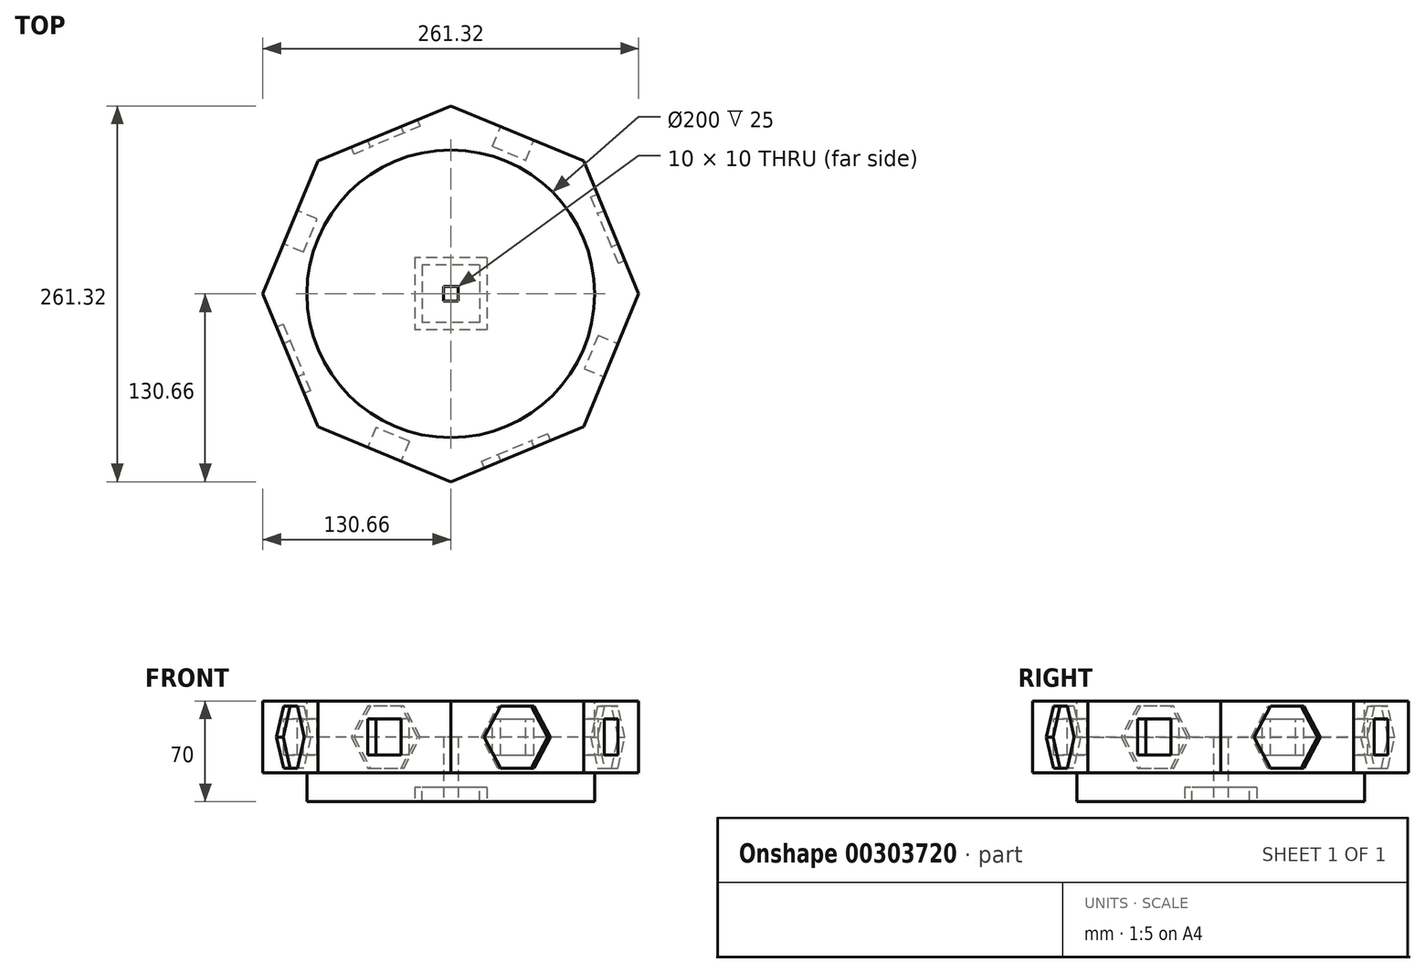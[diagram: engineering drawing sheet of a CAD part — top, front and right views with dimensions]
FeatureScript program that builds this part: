
annotation { "Feature Type Name" : "Feature", "Feature Type Description" : "" }
export const myFeature = defineFeature(function(context is Context, id is Id, definition is map)
    precondition{}
    {
        {
            var Q0;
            Q0=qCreatedBy(makeId("Top.planeOp"),FACE);
            var sketch = newSketch(context, id + "F0", { "sketchPlane" : qUnion([Q0])});
            skCircle(sketch, "E0.cCircle", {"center": v(0, 0) * mm, "radius": 130.66 * mm, "construction": true});
            skLineSegment(sketch, "E0.0", {"start": v(0, -130.66) * mm, "end": v(-92.39, -92.39) * mm});
            skLineSegment(sketch, "E0.1", {"start": v(-92.39, -92.39) * mm, "end": v(-130.66, 0) * mm});
            skLineSegment(sketch, "E0.2", {"start": v(-130.66, 0) * mm, "end": v(-92.39, 92.39) * mm});
            skLineSegment(sketch, "E0.3", {"start": v(-92.39, 92.39) * mm, "end": v(0, 130.66) * mm});
            skLineSegment(sketch, "E0.4", {"start": v(0, 130.66) * mm, "end": v(92.39, 92.39) * mm});
            skLineSegment(sketch, "E0.5", {"start": v(92.39, 92.39) * mm, "end": v(130.66, 0) * mm});
            skLineSegment(sketch, "E0.6", {"start": v(130.66, 0) * mm, "end": v(92.39, -92.39) * mm});
            skLineSegment(sketch, "E0.7", {"start": v(92.39, -92.39) * mm, "end": v(0, -130.66) * mm});
            skSolve(sketch);
        }
        {
            var Q0;
            Q0=makeQuery(id+"F0.imprint","IMPRINT",FACE,{"disambiguationData":[TD([[makeQuery(id+"F0.imprint","IMPRINT",EDGE,{"derivedFrom":sQuery(id+"F0.wireOp",EDGE,"E0.0")}),-1.0]])]});
            extrude(context, id + "F1", {"entities" : qUnion([Q0]), "depth" : 50 * mm});
        }
        {
            var Q0;
            Q0=makeQuery(id+"F1.opExtrude","SWEPT_FACE",FACE,{"disambiguationData":[OSD([sQuery(id+"F0.wireOp",EDGE,"E0.0")])]});
            var sketch = newSketch(context, id + "F2", { "sketchPlane" : qUnion([Q0])});
            skLineSegment(sketch, "E1.bottom", {"start": v(12.5, 12.5) * mm, "end": v(-12.5, 12.5) * mm});
            skLineSegment(sketch, "E1.top", {"start": v(12.5, 37.5) * mm, "end": v(-12.5, 37.5) * mm});
            skLineSegment(sketch, "E1.left", {"start": v(12.5, 12.5) * mm, "end": v(12.5, 37.5) * mm});
            skLineSegment(sketch, "E1.right", {"start": v(-12.5, 12.5) * mm, "end": v(-12.5, 37.5) * mm});
            skPoint(sketch, "E1.middle", {"position": v(0, 25) * mm});
            skPoint(sketch, "E1.middle.positionSnap0", {"position": v(-50, 25) * mm});
            skPoint(sketch, "E1.centerSnap0", {"position": v(-50, 25) * mm});
            skSolve(sketch);
        }
        {
            var Q0;
            Q0=makeQuery(id+"F2.imprint","IMPRINT",FACE,{"disambiguationData":[TD([[makeQuery(id+"F2.imprint","IMPRINT",EDGE,{"derivedFrom":sQuery(id+"F2.wireOp",EDGE,"E1.bottom")}),-1.0]])]});
            extrude(context, id + "F3", {"entities" : qUnion([Q0]), "operationType" : NewBodyOperationType.REMOVE, "oppositeDirection" : true, "depth" : 15 * mm});
        }
        {
            var Q0;
            Q0=makeQuery(id+"F1.opExtrude","SWEPT_FACE",FACE,{"disambiguationData":[OSD([sQuery(id+"F0.wireOp",EDGE,"E0.2")])]});
            var sketch = newSketch(context, id + "F4", { "sketchPlane" : qUnion([Q0])});
            skLineSegment(sketch, "E2.bottom", {"start": v(12.5, 12.5) * mm, "end": v(-12.5, 12.5) * mm});
            skLineSegment(sketch, "E2.top", {"start": v(12.5, 37.5) * mm, "end": v(-12.5, 37.5) * mm});
            skLineSegment(sketch, "E2.left", {"start": v(12.5, 12.5) * mm, "end": v(12.5, 37.5) * mm});
            skLineSegment(sketch, "E2.right", {"start": v(-12.5, 12.5) * mm, "end": v(-12.5, 37.5) * mm});
            skPoint(sketch, "E2.middle", {"position": v(0, 25) * mm});
            skPoint(sketch, "E2.middle.positionSnap0", {"position": v(-50, 25) * mm});
            skPoint(sketch, "E2.centerSnap0", {"position": v(-50, 25) * mm});
            skSolve(sketch);
        }
        {
            var Q0;
            Q0=makeQuery(id+"F4.imprint","IMPRINT",FACE,{"disambiguationData":[TD([[makeQuery(id+"F4.imprint","IMPRINT",EDGE,{"derivedFrom":sQuery(id+"F4.wireOp",EDGE,"E2.bottom")}),-1.0]])]});
            extrude(context, id + "F5", {"entities" : qUnion([Q0]), "operationType" : NewBodyOperationType.REMOVE, "oppositeDirection" : true, "depth" : 15 * mm});
        }
        {
            var Q0;
            Q0=makeQuery(id+"F1.opExtrude","SWEPT_FACE",FACE,{"disambiguationData":[OSD([sQuery(id+"F0.wireOp",EDGE,"E0.4")])]});
            var sketch = newSketch(context, id + "F6", { "sketchPlane" : qUnion([Q0])});
            skLineSegment(sketch, "E3.bottom", {"start": v(12.5, 12.5) * mm, "end": v(-12.5, 12.5) * mm});
            skLineSegment(sketch, "E3.top", {"start": v(12.5, 37.5) * mm, "end": v(-12.5, 37.5) * mm});
            skLineSegment(sketch, "E3.left", {"start": v(12.5, 12.5) * mm, "end": v(12.5, 37.5) * mm});
            skLineSegment(sketch, "E3.right", {"start": v(-12.5, 12.5) * mm, "end": v(-12.5, 37.5) * mm});
            skPoint(sketch, "E3.middle", {"position": v(0, 25) * mm});
            skPoint(sketch, "E3.middle.positionSnap0", {"position": v(-50, 25) * mm});
            skPoint(sketch, "E3.centerSnap0", {"position": v(-50, 25) * mm});
            skSolve(sketch);
        }
        {
            var Q0;
            Q0=makeQuery(id+"F6.imprint","IMPRINT",FACE,{"disambiguationData":[TD([[makeQuery(id+"F6.imprint","IMPRINT",EDGE,{"derivedFrom":sQuery(id+"F6.wireOp",EDGE,"E3.bottom")}),-1.0]])]});
            extrude(context, id + "F7", {"entities" : qUnion([Q0]), "operationType" : NewBodyOperationType.REMOVE, "oppositeDirection" : true, "depth" : 15 * mm});
        }
        {
            var Q0;
            Q0=makeQuery(id+"F1.opExtrude","SWEPT_FACE",FACE,{"disambiguationData":[OSD([sQuery(id+"F0.wireOp",EDGE,"E0.6")])]});
            var sketch = newSketch(context, id + "F8", { "sketchPlane" : qUnion([Q0])});
            skLineSegment(sketch, "E4.bottom", {"start": v(12.5, 12.5) * mm, "end": v(-12.5, 12.5) * mm});
            skLineSegment(sketch, "E4.top", {"start": v(12.5, 37.5) * mm, "end": v(-12.5, 37.5) * mm});
            skLineSegment(sketch, "E4.left", {"start": v(12.5, 12.5) * mm, "end": v(12.5, 37.5) * mm});
            skLineSegment(sketch, "E4.right", {"start": v(-12.5, 12.5) * mm, "end": v(-12.5, 37.5) * mm});
            skPoint(sketch, "E4.middle", {"position": v(0, 25) * mm});
            skPoint(sketch, "E4.middle.positionSnap0", {"position": v(-50, 25) * mm});
            skPoint(sketch, "E4.centerSnap0", {"position": v(-50, 25) * mm});
            skSolve(sketch);
        }
        {
            var Q0;
            Q0=makeQuery(id+"F8.imprint","IMPRINT",FACE,{"disambiguationData":[TD([[makeQuery(id+"F8.imprint","IMPRINT",EDGE,{"derivedFrom":sQuery(id+"F8.wireOp",EDGE,"E4.bottom")}),-1.0]])]});
            extrude(context, id + "F9", {"entities" : qUnion([Q0]), "operationType" : NewBodyOperationType.REMOVE, "oppositeDirection" : true, "depth" : 15 * mm});
        }
        {
            var Q0;
            Q0=makeQuery(id+"F1.opExtrude","SWEPT_FACE",FACE,{"disambiguationData":[OSD([sQuery(id+"F0.wireOp",EDGE,"E0.7")])]});
            var sketch = newSketch(context, id + "F10", { "sketchPlane" : qUnion([Q0])});
            skCircle(sketch, "E5.cCircle", {"center": v(0, 25) * mm, "radius": 21.65 * mm, "construction": true});
            skPoint(sketch, "E5.cCircle.centerSnap0", {"position": v(-50, 25) * mm});
            skLineSegment(sketch, "E5.0", {"start": v(25, 25) * mm, "end": v(12.5, 3.35) * mm});
            skLineSegment(sketch, "E5.1", {"start": v(12.5, 3.35) * mm, "end": v(-12.5, 3.35) * mm});
            skLineSegment(sketch, "E5.2", {"start": v(-12.5, 3.35) * mm, "end": v(-25, 25) * mm});
            skLineSegment(sketch, "E5.3", {"start": v(-25, 25) * mm, "end": v(-12.5, 46.65) * mm});
            skLineSegment(sketch, "E5.4", {"start": v(-12.5, 46.65) * mm, "end": v(12.5, 46.65) * mm});
            skLineSegment(sketch, "E5.5", {"start": v(12.5, 46.65) * mm, "end": v(25, 25) * mm});
            skPoint(sketch, "E5.0.midPoint", {"position": v(18.75, 14.17) * mm});
            skSolve(sketch);
        }
        {
            var Q0;
            Q0=makeQuery(id+"F10.imprint","IMPRINT",FACE,{"disambiguationData":[TD([[makeQuery(id+"F10.imprint","IMPRINT",EDGE,{"derivedFrom":sQuery(id+"F10.wireOp",EDGE,"E5.0")}),-1.0]])]});
            extrude(context, id + "F11", {"entities" : qUnion([Q0]), "operationType" : NewBodyOperationType.REMOVE, "oppositeDirection" : true, "depth" : 5 * mm});
        }
        {
            var Q0;
            Q0=makeQuery(id+"F1.opExtrude","SWEPT_FACE",FACE,{"disambiguationData":[OSD([sQuery(id+"F0.wireOp",EDGE,"E0.5")])]});
            var sketch = newSketch(context, id + "F12", { "sketchPlane" : qUnion([Q0])});
            skCircle(sketch, "E6.cCircle", {"center": v(0, 25) * mm, "radius": 21.65 * mm, "construction": true});
            skPoint(sketch, "E6.cCircle.centerSnap0", {"position": v(0, 50) * mm});
            skPoint(sketch, "E6.cCircle.centerSnap1", {"position": v(-50, 25) * mm});
            skLineSegment(sketch, "E6.0", {"start": v(25, 25) * mm, "end": v(12.5, 3.35) * mm});
            skLineSegment(sketch, "E6.1", {"start": v(12.5, 3.35) * mm, "end": v(-12.5, 3.35) * mm});
            skLineSegment(sketch, "E6.2", {"start": v(-12.5, 3.35) * mm, "end": v(-25, 25) * mm});
            skLineSegment(sketch, "E6.3", {"start": v(-25, 25) * mm, "end": v(-12.5, 46.65) * mm});
            skLineSegment(sketch, "E6.4", {"start": v(-12.5, 46.65) * mm, "end": v(12.5, 46.65) * mm});
            skLineSegment(sketch, "E6.5", {"start": v(12.5, 46.65) * mm, "end": v(25, 25) * mm});
            skPoint(sketch, "E6.0.midPoint", {"position": v(18.75, 14.17) * mm});
            skSolve(sketch);
        }
        {
            var Q0;
            Q0=makeQuery(id+"F12.imprint","IMPRINT",FACE,{"disambiguationData":[TD([[makeQuery(id+"F12.imprint","IMPRINT",EDGE,{"derivedFrom":sQuery(id+"F12.wireOp",EDGE,"E6.0")}),-1.0]])]});
            extrude(context, id + "F13", {"entities" : qUnion([Q0]), "operationType" : NewBodyOperationType.REMOVE, "oppositeDirection" : true, "depth" : 5 * mm});
        }
        {
            var Q0;
            Q0=makeQuery(id+"F1.opExtrude","SWEPT_FACE",FACE,{"disambiguationData":[OSD([sQuery(id+"F0.wireOp",EDGE,"E0.1")])]});
            var sketch = newSketch(context, id + "F14", { "sketchPlane" : qUnion([Q0])});
            skCircle(sketch, "E7.cCircle", {"center": v(0, 25) * mm, "radius": 21.65 * mm, "construction": true});
            skPoint(sketch, "E7.cCircle.centerSnap0", {"position": v(-50, 25) * mm});
            skLineSegment(sketch, "E7.0", {"start": v(-12.5, 46.65) * mm, "end": v(12.5, 46.65) * mm});
            skLineSegment(sketch, "E7.1", {"start": v(12.5, 46.65) * mm, "end": v(25, 25) * mm});
            skLineSegment(sketch, "E7.2", {"start": v(25, 25) * mm, "end": v(12.5, 3.35) * mm});
            skLineSegment(sketch, "E7.3", {"start": v(12.5, 3.35) * mm, "end": v(-12.5, 3.35) * mm});
            skLineSegment(sketch, "E7.4", {"start": v(-12.5, 3.35) * mm, "end": v(-25, 25) * mm});
            skLineSegment(sketch, "E7.5", {"start": v(-25, 25) * mm, "end": v(-12.5, 46.65) * mm});
            skPoint(sketch, "E7.0.midPoint", {"position": v(0, 46.65) * mm});
            skSolve(sketch);
        }
        {
            var Q0;
            Q0=makeQuery(id+"F14.imprint","IMPRINT",FACE,{"disambiguationData":[TD([[makeQuery(id+"F14.imprint","IMPRINT",EDGE,{"derivedFrom":sQuery(id+"F14.wireOp",EDGE,"E7.0")}),-1.0]])]});
            extrude(context, id + "F15", {"entities" : qUnion([Q0]), "operationType" : NewBodyOperationType.REMOVE, "oppositeDirection" : true, "depth" : 5 * mm});
        }
        {
            var Q0;
            Q0=makeQuery(id+"F1.opExtrude","SWEPT_FACE",FACE,{"disambiguationData":[OSD([sQuery(id+"F0.wireOp",EDGE,"E0.3")])]});
            var sketch = newSketch(context, id + "F16", { "sketchPlane" : qUnion([Q0])});
            skCircle(sketch, "E8.cCircle", {"center": v(0, 25) * mm, "radius": 21.65 * mm, "construction": true});
            skPoint(sketch, "E8.cCircle.centerSnap0", {"position": v(-50, 25) * mm});
            skPoint(sketch, "E8.cCircle.perimeterSnap0", {"position": v(0, 50) * mm});
            skLineSegment(sketch, "E8.0", {"start": v(-12.5, 46.65) * mm, "end": v(12.5, 46.65) * mm});
            skLineSegment(sketch, "E8.1", {"start": v(12.5, 46.65) * mm, "end": v(25, 25) * mm});
            skLineSegment(sketch, "E8.2", {"start": v(25, 25) * mm, "end": v(12.5, 3.35) * mm});
            skLineSegment(sketch, "E8.3", {"start": v(12.5, 3.35) * mm, "end": v(-12.5, 3.35) * mm});
            skLineSegment(sketch, "E8.4", {"start": v(-12.5, 3.35) * mm, "end": v(-25, 25) * mm});
            skLineSegment(sketch, "E8.5", {"start": v(-25, 25) * mm, "end": v(-12.5, 46.65) * mm});
            skPoint(sketch, "E8.0.midPoint", {"position": v(0, 46.65) * mm});
            skPoint(sketch, "E8.0.midPoint.positionSnap0", {"position": v(0, 50) * mm});
            skSolve(sketch);
        }
        {
            var Q0;
            Q0=makeQuery(id+"F16.imprint","IMPRINT",FACE,{"disambiguationData":[TD([[makeQuery(id+"F16.imprint","IMPRINT",EDGE,{"derivedFrom":sQuery(id+"F16.wireOp",EDGE,"E8.0")}),-1.0]])]});
            extrude(context, id + "F17", {"entities" : qUnion([Q0]), "operationType" : NewBodyOperationType.REMOVE, "oppositeDirection" : true, "depth" : 5 * mm});
        }
        {
            var Q0;
            Q0=makeQuery(id+"F1.opExtrude","CAP_FACE",FACE,{"disambiguationData":[OSD([sQuery(id+"F0.wireOp",EDGE,"E0.0"),sQuery(id+"F0.wireOp",EDGE,"E0.1"),sQuery(id+"F0.wireOp",EDGE,"E0.2"),sQuery(id+"F0.wireOp",EDGE,"E0.3"),sQuery(id+"F0.wireOp",EDGE,"E0.4"),sQuery(id+"F0.wireOp",EDGE,"E0.5"),sQuery(id+"F0.wireOp",EDGE,"E0.6"),sQuery(id+"F0.wireOp",EDGE,"E0.7")])],"isStart":false});
            var sketch = newSketch(context, id + "F18", { "sketchPlane" : qUnion([Q0])});
            skCircle(sketch, "E9", {"center": v(0, 0) * mm, "radius": 100 * mm});
            skSolve(sketch);
        }
        {
            var Q0;
            Q0=qSketchRegion(id+"F18",true);
            extrude(context, id + "F19", {"entities" : qUnion([Q0]), "operationType" : NewBodyOperationType.REMOVE, "oppositeDirection" : true, "depth" : 25 * mm});
        }
        {
            var Q0;
            Q0=makeQuery(id+"F1.opExtrude","CAP_FACE",FACE,{"disambiguationData":[OSD([sQuery(id+"F0.wireOp",EDGE,"E0.0"),sQuery(id+"F0.wireOp",EDGE,"E0.1"),sQuery(id+"F0.wireOp",EDGE,"E0.2"),sQuery(id+"F0.wireOp",EDGE,"E0.3"),sQuery(id+"F0.wireOp",EDGE,"E0.4"),sQuery(id+"F0.wireOp",EDGE,"E0.5"),sQuery(id+"F0.wireOp",EDGE,"E0.6"),sQuery(id+"F0.wireOp",EDGE,"E0.7")])],"isStart":true});
            var sketch = newSketch(context, id + "F20", { "sketchPlane" : qUnion([Q0])});
            skCircle(sketch, "E10", {"center": v(0, 0) * mm, "radius": 100 * mm});
            skSolve(sketch);
        }
        {
            var Q0;
            Q0=qSketchRegion(id+"F20",true);
            extrude(context, id + "F21", {"entities" : qUnion([Q0]), "operationType" : NewBodyOperationType.ADD, "depth" : 20 * mm});
        }
        {
            var Q0;
            Q0=makeQuery(id+"F1.opExtrude","SWEPT_BODY",BODY,{"disambiguationData":[OSD([sQuery(id+"F0.wireOp",EDGE,"E0.0"),sQuery(id+"F0.wireOp",EDGE,"E0.1"),sQuery(id+"F0.wireOp",EDGE,"E0.2"),sQuery(id+"F0.wireOp",EDGE,"E0.3"),sQuery(id+"F0.wireOp",EDGE,"E0.4"),sQuery(id+"F0.wireOp",EDGE,"E0.5"),sQuery(id+"F0.wireOp",EDGE,"E0.6"),sQuery(id+"F0.wireOp",EDGE,"E0.7")])]});
            transform(context, id + "F22", {"entities" : qUnion([Q0]), "transformType" : TransformType.TRANSLATION_3D, "dx" : 0 * mm, "dy" : 0 * mm, "dz" : 10 * mm, "makeCopy" : false});
        }
        {
            var Q0;
            Q0=makeQuery(id+"F21.opExtrude","CAP_FACE",FACE,{"disambiguationData":[OSD([sQuery(id+"F20.wireOp",EDGE,"E10")])],"isStart":false});
            var sketch = newSketch(context, id + "F23", { "sketchPlane" : qUnion([Q0])});
            skLineSegment(sketch, "E11.bottom", {"start": v(25, -25) * mm, "end": v(-25, -25) * mm});
            skLineSegment(sketch, "E11.top", {"start": v(25, 25) * mm, "end": v(-25, 25) * mm});
            skLineSegment(sketch, "E11.left", {"start": v(25, -25) * mm, "end": v(25, 25) * mm});
            skLineSegment(sketch, "E11.right", {"start": v(-25, -25) * mm, "end": v(-25, 25) * mm});
            skPoint(sketch, "E11.middle", {"position": v(0, 0) * mm});
            skSolve(sketch);
        }
        {
            var Q0;
            Q0=makeQuery(id+"F23.imprint","IMPRINT",FACE,{"disambiguationData":[TD([[makeQuery(id+"F23.imprint","IMPRINT",EDGE,{"derivedFrom":sQuery(id+"F23.wireOp",EDGE,"E11.bottom")}),-1.0]])]});
            extrude(context, id + "F24", {"entities" : qUnion([Q0]), "operationType" : NewBodyOperationType.REMOVE, "oppositeDirection" : true, "depth" : 10 * mm});
        }
        {
            var Q0;
            Q0=makeQuery(id+"F24.boolean.opBoolean","COPY",FACE,{"derivedFrom":makeQuery(id+"F24.opExtrude","CAP_FACE",FACE,{"disambiguationData":[OSD([sQuery(id+"F23.wireOp",EDGE,"E11.bottom"),sQuery(id+"F23.wireOp",EDGE,"E11.top"),sQuery(id+"F23.wireOp",EDGE,"E11.left"),sQuery(id+"F23.wireOp",EDGE,"E11.right")])],"isStart":false})});
            var sketch = newSketch(context, id + "F25", { "sketchPlane" : qUnion([Q0])});
            skLineSegment(sketch, "E12.bottom", {"start": v(20, -20) * mm, "end": v(-20, -20) * mm});
            skLineSegment(sketch, "E12.top", {"start": v(20, 20) * mm, "end": v(-20, 20) * mm});
            skLineSegment(sketch, "E12.left", {"start": v(20, -20) * mm, "end": v(20, 20) * mm});
            skLineSegment(sketch, "E12.right", {"start": v(-20, -20) * mm, "end": v(-20, 20) * mm});
            skPoint(sketch, "E12.middle", {"position": v(0, 0) * mm});
            skSolve(sketch);
        }
        {
            var Q0;
            Q0 = qSketchRegion(id + "F25", true);
            extrude(context, id + "F26", {"entities" : qUnion([Q0]), "operationType" : NewBodyOperationType.ADD, "depth" : 10 * mm});
        }
        {
            var Q0;
            Q0=makeQuery(id+"F26.opExtrude","CAP_FACE",FACE,{"disambiguationData":[OSD([sQuery(id+"F25.wireOp",EDGE,"E12.bottom"),sQuery(id+"F25.wireOp",EDGE,"E12.top"),sQuery(id+"F25.wireOp",EDGE,"E12.left"),sQuery(id+"F25.wireOp",EDGE,"E12.right")])],"isStart":false});
            var sketch = newSketch(context, id + "F27", { "sketchPlane" : qUnion([Q0])});
            skLineSegment(sketch, "E13.bottom", {"start": v(5, -5) * mm, "end": v(-5, -5) * mm});
            skLineSegment(sketch, "E13.top", {"start": v(5, 5) * mm, "end": v(-5, 5) * mm});
            skLineSegment(sketch, "E13.left", {"start": v(5, -5) * mm, "end": v(5, 5) * mm});
            skLineSegment(sketch, "E13.right", {"start": v(-5, -5) * mm, "end": v(-5, 5) * mm});
            skPoint(sketch, "E13.middle", {"position": v(0, 0) * mm});
            skSolve(sketch);
        }
        {
            var Q0;
            Q0=makeQuery(id+"F27.imprint","IMPRINT",FACE,{"disambiguationData":[TD([[makeQuery(id+"F27.imprint","IMPRINT",EDGE,{"derivedFrom":sQuery(id+"F27.wireOp",EDGE,"E13.bottom")}),-1.0]])]});
            extrude(context, id + "F28", {"entities" : qUnion([Q0]), "operationType" : NewBodyOperationType.REMOVE, "oppositeDirection" : true, "depth" : 45 * mm});
        }
    });
